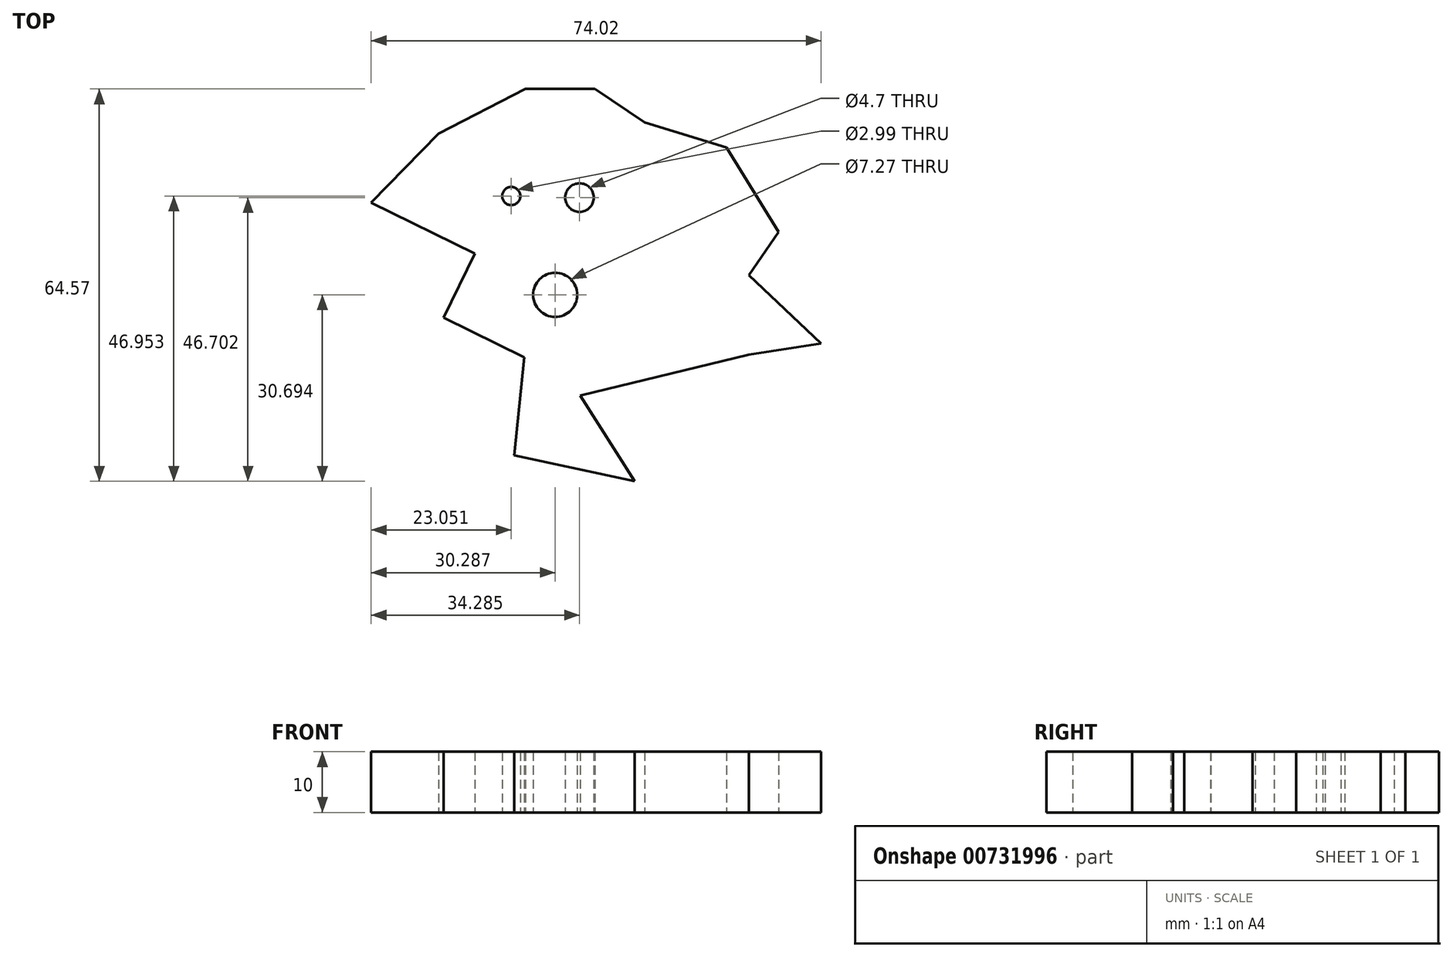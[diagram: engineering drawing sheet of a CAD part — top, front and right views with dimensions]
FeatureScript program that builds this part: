
annotation { "Feature Type Name" : "Feature", "Feature Type Description" : "" }
export const myFeature = defineFeature(function(context is Context, id is Id, definition is map)
    precondition{}
    {
        {
            var Q0;
            Q0=qCreatedBy(makeId("Top.planeOp"),FACE);
            var sketch = newSketch(context, id + "F0", { "sketchPlane" : qUnion([Q0])});
            skLineSegment(sketch, "E0", {"start": v(-41.28, 39.33) * mm, "end": v(-26.97, 46.7) * mm});
            skLineSegment(sketch, "E1", {"start": v(-26.97, 46.7) * mm, "end": v(-15.53, 46.7) * mm});
            skLineSegment(sketch, "E2", {"start": v(-15.53, 46.7) * mm, "end": v(-7.36, 41.17) * mm});
            skLineSegment(sketch, "E3", {"start": v(-7.36, 41.17) * mm, "end": v(6.13, 37.09) * mm});
            skLineSegment(sketch, "E4", {"start": v(6.13, 37.09) * mm, "end": v(14.71, 23.2) * mm});
            skLineSegment(sketch, "E5", {"start": v(14.71, 23.2) * mm, "end": v(9.8, 16.04) * mm});
            skLineSegment(sketch, "E6", {"start": v(9.8, 16.04) * mm, "end": v(21.66, 4.8) * mm});
            skLineSegment(sketch, "E7", {"start": v(21.66, 4.8) * mm, "end": v(9.8, 2.96) * mm});
            skLineSegment(sketch, "E8", {"start": v(9.8, 2.96) * mm, "end": v(-17.98, -3.78) * mm});
            skLineSegment(sketch, "E9", {"start": v(-17.98, -3.78) * mm, "end": v(-9, -17.88) * mm});
            skLineSegment(sketch, "E10", {"start": v(-9, -17.88) * mm, "end": v(-28.81, -13.59) * mm});
            skLineSegment(sketch, "E11", {"start": v(-28.81, -13.59) * mm, "end": v(-27.18, 2.55) * mm});
            skLineSegment(sketch, "E12", {"start": v(-27.18, 2.55) * mm, "end": v(-40.46, 9.1) * mm});
            skLineSegment(sketch, "E13", {"start": v(-40.46, 9.1) * mm, "end": v(-35.3, 19.59) * mm});
            skLineSegment(sketch, "E14", {"start": v(-35.3, 19.59) * mm, "end": v(-52.36, 27.99) * mm});
            skLineSegment(sketch, "E15", {"start": v(-52.36, 27.99) * mm, "end": v(-41.28, 39.33) * mm});
            skCircle(sketch, "E16", {"center": v(-29.3, 29.07) * mm, "radius": 1.5 * mm});
            skCircle(sketch, "E17", {"center": v(-18.07, 28.82) * mm, "radius": 2.35 * mm});
            skCircle(sketch, "E18", {"center": v(-22.07, 12.81) * mm, "radius": 3.63 * mm});
            skPoint(sketch, "E19.center", {"position": v(0, 0) * mm});
            skCircle(sketch, "E20", {"center": v(-119.72, 44.98) * mm, "radius": 10.38 * mm});
            skCircle(sketch, "E21.1.0", {"center": v(-141.62, 41.1) * mm, "radius": 10.38 * mm});
            skCircle(sketch, "E21.2.0", {"center": v(-162.52, 48.7) * mm, "radius": 10.38 * mm});
            skPoint(sketch, "E21.center", {"position": v(-137.9, 83.9) * mm});
            skLineSegment(sketch, "E21.anchor1", {"start": v(-137.9, 83.9) * mm, "end": v(-119.72, 44.98) * mm, "construction": true});
            skLineSegment(sketch, "E21.anchor2", {"start": v(-137.9, 83.9) * mm, "end": v(-162.52, 48.7) * mm, "construction": true});
            skSolve(sketch);
        }
        {
            var Q0;
            Q0=makeQuery(id+"F0.imprint","IMPRINT",FACE,{"disambiguationData":[TD([[makeQuery(id+"F0.imprint","IMPRINT",EDGE,{"derivedFrom":sQuery(id+"F0.wireOp",EDGE,"E0")}),-1.0]])]});
            extrude(context, id + "F1", {"entities" : qUnion([Q0]), "depth" : 10 * mm, "offsetDistance" : 25 * mm});
        }
    });
